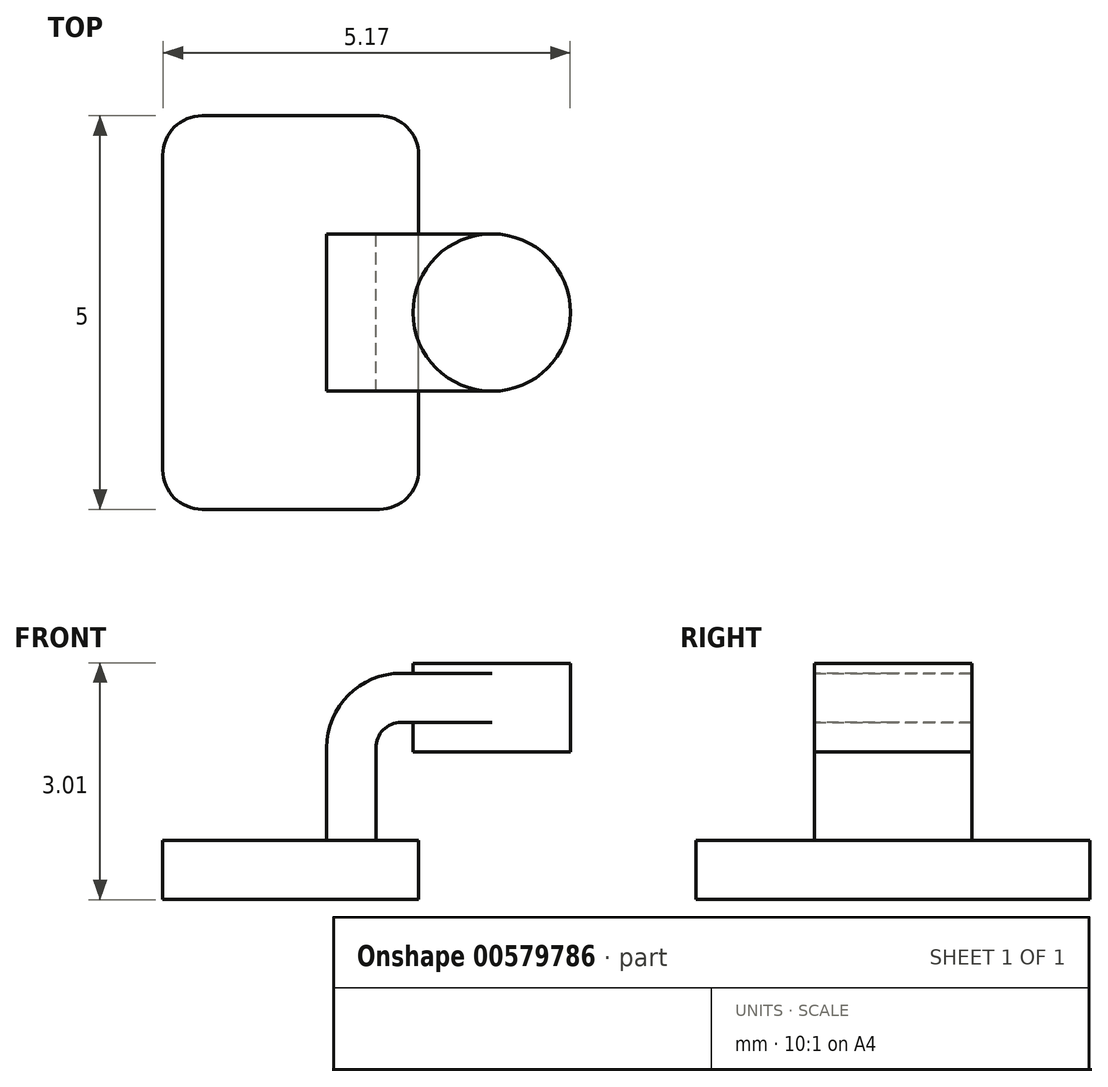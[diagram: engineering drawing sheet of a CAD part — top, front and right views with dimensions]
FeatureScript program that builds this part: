
annotation { "Feature Type Name" : "Feature", "Feature Type Description" : "" }
export const myFeature = defineFeature(function(context is Context, id is Id, definition is map)
    precondition{}
    {
        {
            var Q0;
            Q0=qCreatedBy(makeId("Front.planeOp"),FACE);
            var sketch = newSketch(context, id + "F0", { "sketchPlane" : qUnion([Q0])});
            skLineSegment(sketch, "E0.bottom", {"start": v(-1.63, -0.37) * mm, "end": v(1.63, -0.37) * mm});
            skLineSegment(sketch, "E0.top", {"start": v(-1.63, 0.37) * mm, "end": v(1.63, 0.37) * mm});
            skLineSegment(sketch, "E0.left", {"start": v(-1.63, -0.37) * mm, "end": v(-1.63, 0.37) * mm});
            skLineSegment(sketch, "E0.right", {"start": v(1.63, -0.37) * mm, "end": v(1.63, 0.37) * mm});
            skPoint(sketch, "E0.middle", {"position": v(0, 0) * mm});
            skLineSegment(sketch, "E1.bottom", {"start": v(3.55, 1.5) * mm, "end": v(1.55, 1.5) * mm});
            skLineSegment(sketch, "E1.top", {"start": v(3.55, 2.63) * mm, "end": v(1.55, 2.62) * mm});
            skLineSegment(sketch, "E1.left", {"start": v(3.55, 1.5) * mm, "end": v(3.55, 2.63) * mm});
            skLineSegment(sketch, "E1.right", {"start": v(1.55, 1.5) * mm, "end": v(1.55, 2.62) * mm});
            skLineSegment(sketch, "E2", {"start": v(1.08, 0.37) * mm, "end": v(1.08, 1.55) * mm});
            skArc(sketch, "E3", {"start": v(1.08, 1.55) * mm, "mid": v(1.18, 1.78) * mm, "end": v(1.4, 1.87) * mm});
            skLineSegment(sketch, "E4", {"start": v(1.4, 1.87) * mm, "end": v(2.55, 1.87) * mm});
            skPoint(sketch, "E5", {"position": v(2.55, 1.5) * mm});
            skLineSegment(sketch, "E6", {"start": v(2.55, 1.5) * mm, "end": v(2.55, 2.62) * mm});
            skLineSegment(sketch, "E7.0", {"start": v(1.4, 2.5) * mm, "end": v(2.55, 2.5) * mm});
            skArc(sketch, "E7.1", {"start": v(0.46, 1.55) * mm, "mid": v(0.73, 2.22) * mm, "end": v(1.4, 2.5) * mm});
            skLineSegment(sketch, "E7.2", {"start": v(0.46, 0.37) * mm, "end": v(0.46, 1.55) * mm});
            skFitSpline(sketch, "E8", {"points": [v(-1.63, 0.37) * mm, v(1.4, 2.5) * mm], "startDerivative": vector(2.14, 3.26) * mm, "endDerivative": vector(4.7, 0.02) * mm});
            skSolve(sketch);
        }
        {
            var Q0;
            Q0=makeQuery(id+"F0.imprint","IMPRINT",FACE,{"disambiguationData":[TD([[makeQuery(id+"F0.imprint","IMPRINT",EDGE,{"derivedFrom":sQuery(id+"F0.wireOp",EDGE,"E0.bottom")}),1.0]])]});
            extrude(context, id + "F1", {"entities" : qUnion([Q0]), "endBound" : BoundingType.SYMMETRIC, "depth" : 5 * mm, "offsetDistance" : 25 * mm});
        }
        {
            var Q0;
            {var subQ5=sQuery(id+"F0.wireOp",EDGE,"E2");Q0=makeQuery(id+"F0.imprint","IMPRINT",FACE,{"disambiguationData":[TD([[makeQuery(id+"F0.imprint","IMPRINT",EDGE,{"derivedFrom":subQ5}),1.0]])]});}
            var Q1;
            {var subQ0=sQuery(id+"F0.wireOp",EDGE,"E4");var subQ1=sQuery(id+"F0.wireOp",EDGE,"E1.right");var subQ2=makeQuery(id+"F0.imprint","INTERSECT",VERTEX,{"derivedFrom":[subQ1,subQ0]});Q1=makeQuery(id+"F0.imprint","IMPRINT",FACE,{"disambiguationData":[TD([[makeQuery(id+"F0.imprint","IMPRINT",EDGE,{"disambiguationData":[TD([[subQ2,-1.0]])],"derivedFrom":subQ1}),-1.0]])]});}
            extrude(context, id + "F2", {"entities" : qUnion([Q0, Q1]), "operationType" : NewBodyOperationType.ADD, "endBound" : BoundingType.SYMMETRIC, "depth" : 2 * mm, "offsetDistance" : 25 * mm});
        }
        {
            var Q0;
            {var subQ4=sQuery(id+"F0.wireOp",EDGE,"E7.1");Q0=makeQuery(id+"F0.imprint","IMPRINT",FACE,{"disambiguationData":[TD([[makeQuery(id+"F0.imprint","IMPRINT",EDGE,{"derivedFrom":subQ4}),1.0]])]});}
            extrude(context, id + "F3", {"entities" : qUnion([Q0]), "operationType" : NewBodyOperationType.ADD, "endBound" : BoundingType.SYMMETRIC, "depth" : 1 * mm, "offsetDistance" : 25 * mm});
        }
        {
            var Q0;
            {var subQ0=sQuery(id+"F0.wireOp",EDGE,"E1.left");Q0=makeQuery(id+"F0.imprint","IMPRINT",FACE,{"disambiguationData":[TD([[makeQuery(id+"F0.imprint","IMPRINT",EDGE,{"derivedFrom":subQ0}),1.0]])]});}
            var Q1;
            Q1=sQuery(id+"F0.wireOp",EDGE,"E6");
            revolve(context, id + "F4", {"operationType" : NewBodyOperationType.ADD, "entities" : qUnion([Q0]), "axis" : qUnion([Q1]), "revolveType" : RevolveType.FULL});
        }
        {
            var Q0;
            Q0=makeQuery(id+"F1.opExtrude","CAP_EDGE",EDGE,{"disambiguationData":[OSD([sQuery(id+"F0.wireOp",EDGE,"E0.right")])],"isStart":true});
            var Q1;
            Q1=makeQuery(id+"F1.opExtrude","CAP_EDGE",EDGE,{"disambiguationData":[OSD([sQuery(id+"F0.wireOp",EDGE,"E0.left")])],"isStart":false});
            var Q2;
            Q2=makeQuery(id+"F1.opExtrude","CAP_EDGE",EDGE,{"disambiguationData":[OSD([sQuery(id+"F0.wireOp",EDGE,"E0.right")])],"isStart":false});
            var Q3;
            Q3=makeQuery(id+"F1.opExtrude","CAP_EDGE",EDGE,{"disambiguationData":[OSD([sQuery(id+"F0.wireOp",EDGE,"E0.left")])],"isStart":true});
            fillet(context, id + "F5", {"entities" : qUnion([Q0, Q1, Q2, Q3]), "radius" : .5 * mm, "tangentPropagation" : true, "allowEdgeOverflow" : false});
        }
    });
